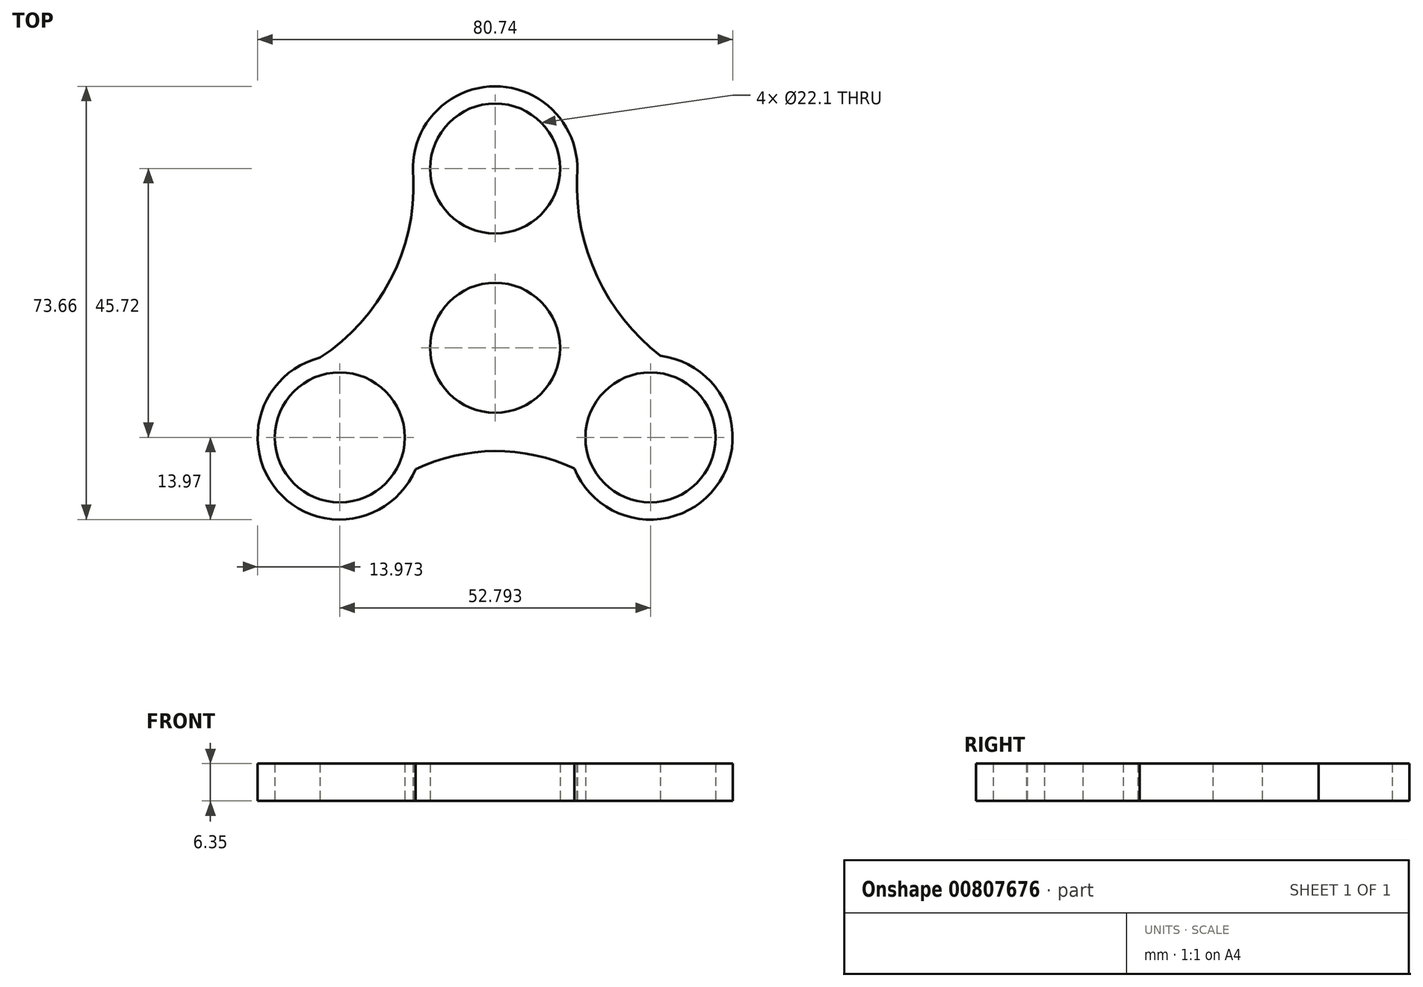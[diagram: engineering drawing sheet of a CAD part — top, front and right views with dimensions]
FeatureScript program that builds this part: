
annotation { "Feature Type Name" : "Feature", "Feature Type Description" : "" }
export const myFeature = defineFeature(function(context is Context, id is Id, definition is map)
    precondition{}
    {
        {
            var Q0;
            Q0=qCreatedBy(makeId("Top.planeOp"),FACE);
            var sketch = newSketch(context, id + "F0", { "sketchPlane" : qUnion([Q0])});
            skCircle(sketch, "E0", {"center": v(0, 0) * mm, "radius": 11.05 * mm});
            skLineSegment(sketch, "E1", {"start": v(0, 0) * mm, "end": v(0, 30.48) * mm});
            skCircle(sketch, "E2", {"center": v(0, 30.48) * mm, "radius": 11.05 * mm});
            skCircle(sketch, "E3.1.0", {"center": v(-26.4, -15.24) * mm, "radius": 11.05 * mm});
            skCircle(sketch, "E3.2.0", {"center": v(26.4, -15.24) * mm, "radius": 11.05 * mm});
            skCircle(sketch, "E4", {"center": v(0, 30.48) * mm, "radius": 13.97 * mm});
            skCircle(sketch, "E5", {"center": v(-26.4, -15.24) * mm, "radius": 13.97 * mm});
            skCircle(sketch, "E6", {"center": v(26.4, -15.24) * mm, "radius": 13.97 * mm});
            skLineSegment(sketch, "E7", {"start": v(0, 30.48) * mm, "end": v(13.97, 30.48) * mm, "construction": true});
            skLineSegment(sketch, "E8", {"start": v(26.4, -15.24) * mm, "end": v(26.4, -1.27) * mm, "construction": true});
            skLineSegment(sketch, "E9", {"start": v(0, 30.48) * mm, "end": v(-13.97, 30.48) * mm, "construction": true});
            skLineSegment(sketch, "E10", {"start": v(-26.4, -15.24) * mm, "end": v(-26.4, -1.27) * mm, "construction": true});
            skLineSegment(sketch, "E11", {"start": v(-26.4, -15.24) * mm, "end": v(-12.43, -15.24) * mm, "construction": true});
            skLineSegment(sketch, "E12", {"start": v(26.4, -15.24) * mm, "end": v(12.43, -15.24) * mm, "construction": true});
            skArc(sketch, "E13", {"start": v(-29.76, -1.68) * mm, "mid": v(-17.45, 12.23) * mm, "end": v(-13.97, 30.48) * mm});
            skArc(sketch, "E14", {"start": v(13.97, 30.48) * mm, "mid": v(17.05, 12.8) * mm, "end": v(28.08, -1.37) * mm});
            skArc(sketch, "E15", {"start": v(13.46, -20.5) * mm, "mid": v(-0.05, -17.57) * mm, "end": v(-13.52, -20.65) * mm});
            skSolve(sketch);
        }
        {
            var Q0;
            Q0 = qSketchRegion(id + "F0", true);
            extrude(context, id + "F1", {"entities" : qUnion([Q0]), "depth" : 6.35 * mm, "offsetDistance" : 25.4 * mm});
        }
    });
